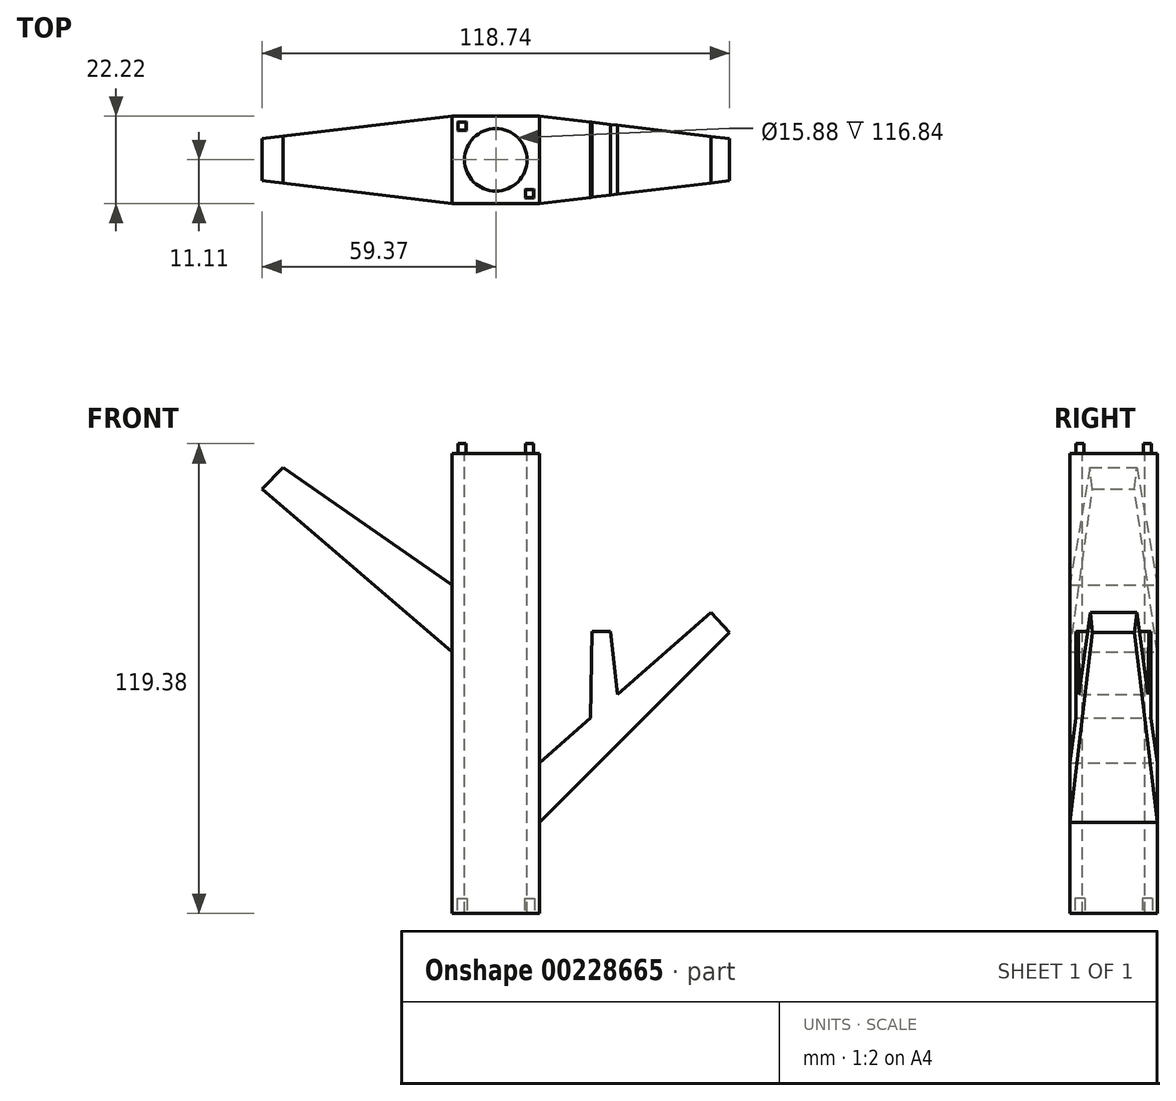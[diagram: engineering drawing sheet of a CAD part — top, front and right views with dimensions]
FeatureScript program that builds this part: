
annotation { "Feature Type Name" : "Feature", "Feature Type Description" : "" }
export const myFeature = defineFeature(function(context is Context, id is Id, definition is map)
    precondition{}
    {
        {
            var Q0;
            Q0=qCreatedBy(makeId("Front.planeOp"),FACE);
            var sketch = newSketch(context, id + "F0", { "sketchPlane" : qUnion([Q0])});
            skLineSegment(sketch, "E0.bottom", {"start": v(11.11, -58.42) * mm, "end": v(-11.11, -58.42) * mm});
            skLineSegment(sketch, "E0.top", {"start": v(11.11, 58.42) * mm, "end": v(-11.11, 58.42) * mm});
            skLineSegment(sketch, "E0.left", {"start": v(11.11, -58.42) * mm, "end": v(11.11, 58.42) * mm});
            skLineSegment(sketch, "E0.right", {"start": v(-11.11, -58.42) * mm, "end": v(-11.11, 58.42) * mm});
            skPoint(sketch, "E0.middle", {"position": v(0, 8.9) * mm});
            skLineSegment(sketch, "E1", {"start": v(0, 17.33) * mm, "end": v(-54.08, 54.94) * mm});
            skLineSegment(sketch, "E2", {"start": v(-54.08, 54.94) * mm, "end": v(-59.37, 49.45) * mm});
            skLineSegment(sketch, "E3", {"start": v(-59.37, 49.45) * mm, "end": v(0, -1.57) * mm});
            skLineSegment(sketch, "E4", {"start": v(0, -1.57) * mm, "end": v(0, 17.33) * mm});
            skLineSegment(sketch, "E5", {"start": v(0, -46.43) * mm, "end": v(59.37, 12.94) * mm});
            skLineSegment(sketch, "E6", {"start": v(59.37, 12.94) * mm, "end": v(54.7, 18.05) * mm});
            skLineSegment(sketch, "E7", {"start": v(54.7, 18.05) * mm, "end": v(0, -29.87) * mm});
            skLineSegment(sketch, "E8", {"start": v(0, -29.87) * mm, "end": v(0, -46.43) * mm});
            skLineSegment(sketch, "E9", {"start": v(24.1, -8.76) * mm, "end": v(24.4, 13.23) * mm});
            skPoint(sketch, "E9.endSnap0", {"position": v(27.35, -5.9) * mm});
            skLineSegment(sketch, "E10", {"start": v(24.4, 13.23) * mm, "end": v(29.13, 13.23) * mm});
            skLineSegment(sketch, "E11", {"start": v(29.13, 13.23) * mm, "end": v(30.88, -2.82) * mm});
            skSolve(sketch);
        }
        {
            var Q0;
            Q0 = qSketchRegion(id + "F0", true);
            extrude(context, id + "F1", {"entities" : qUnion([Q0]), "endBound" : BoundingType.SYMMETRIC, "depth" : 22.22 * mm});
        }
        {
            var Q0;
            Q0=makeQuery(id+"F1.opExtrude","SWEPT_FACE",FACE,{"disambiguationData":[OSD([sQuery(id+"F0.wireOp",EDGE,"E0.top")])]});
            var sketch = newSketch(context, id + "F2", { "sketchPlane" : qUnion([Q0])});
            skCircle(sketch, "E12", {"center": v(0, 0) * mm, "radius": 7.94 * mm});
            skSolve(sketch);
        }
        {
            var Q0;
            Q0 = qSketchRegion(id + "F2", true);
            extrude(context, id + "F3", {"entities" : qUnion([Q0]), "operationType" : NewBodyOperationType.REMOVE, "oppositeDirection" : true, "depth" : 133.1 * mm});
        }
        {
            var Q0;
            Q0=makeQuery(id+"F1.opExtrude","SWEPT_FACE",FACE,{"disambiguationData":[OSD([sQuery(id+"F0.wireOp",EDGE,"E0.top")])]});
            var sketch = newSketch(context, id + "F4", { "sketchPlane" : qUnion([Q0])});
            skLineSegment(sketch, "E13", {"start": v(-11.11, -11.11) * mm, "end": v(-61.55, -5.08) * mm});
            skLineSegment(sketch, "E14", {"start": v(-61.55, -5.08) * mm, "end": v(-61.55, -11.11) * mm});
            skLineSegment(sketch, "E15", {"start": v(-61.55, -11.11) * mm, "end": v(-11.11, -11.11) * mm});
            skLineSegment(sketch, "E16", {"start": v(-11.11, 11.11) * mm, "end": v(-61.55, 5.08) * mm});
            skLineSegment(sketch, "E17", {"start": v(-61.55, 5.08) * mm, "end": v(-61.55, 11.11) * mm});
            skLineSegment(sketch, "E18", {"start": v(-61.55, 11.11) * mm, "end": v(-11.11, 11.11) * mm});
            skLineSegment(sketch, "E19", {"start": v(11.11, -11.11) * mm, "end": v(61.55, -5.08) * mm});
            skLineSegment(sketch, "E20", {"start": v(61.55, -5.08) * mm, "end": v(61.55, -11.11) * mm});
            skLineSegment(sketch, "E21", {"start": v(61.55, -11.11) * mm, "end": v(11.11, -11.11) * mm});
            skLineSegment(sketch, "E22", {"start": v(11.11, 11.11) * mm, "end": v(61.55, 5.08) * mm});
            skLineSegment(sketch, "E23", {"start": v(61.55, 5.08) * mm, "end": v(61.55, 11.11) * mm});
            skLineSegment(sketch, "E24", {"start": v(61.55, 11.11) * mm, "end": v(11.11, 11.11) * mm});
            skSolve(sketch);
        }
        {
            var Q0;
            Q0 = qSketchRegion(id + "F4", true);
            extrude(context, id + "F5", {"entities" : qUnion([Q0]), "operationType" : NewBodyOperationType.REMOVE, "oppositeDirection" : true, "depth" : 135.64 * mm});
        }
        {
            var Q0;
            Q0=makeQuery(id+"F1.opExtrude","SWEPT_FACE",FACE,{"disambiguationData":[OSD([sQuery(id+"F0.wireOp",EDGE,"E0.bottom")])]});
            var sketch = newSketch(context, id + "F6", { "sketchPlane" : qUnion([Q0])});
            skLineSegment(sketch, "E25.bottom", {"start": v(7.3, 7.3) * mm, "end": v(9.84, 7.3) * mm});
            skLineSegment(sketch, "E25.top", {"start": v(7.3, 9.84) * mm, "end": v(9.84, 9.84) * mm});
            skLineSegment(sketch, "E25.left", {"start": v(7.3, 7.3) * mm, "end": v(7.3, 9.84) * mm});
            skLineSegment(sketch, "E25.right", {"start": v(9.84, 7.3) * mm, "end": v(9.84, 9.84) * mm});
            skPoint(sketch, "E25.middle", {"position": v(8.57, 8.57) * mm});
            skLineSegment(sketch, "E26.bottom", {"start": v(-9.84, -9.84) * mm, "end": v(-7.3, -9.84) * mm});
            skLineSegment(sketch, "E26.top", {"start": v(-9.84, -7.3) * mm, "end": v(-7.3, -7.3) * mm});
            skLineSegment(sketch, "E26.left", {"start": v(-9.84, -9.84) * mm, "end": v(-9.84, -7.3) * mm});
            skLineSegment(sketch, "E26.right", {"start": v(-7.3, -9.84) * mm, "end": v(-7.3, -7.3) * mm});
            skPoint(sketch, "E26.middle", {"position": v(-8.57, -8.57) * mm});
            skSolve(sketch);
        }
        {
            var Q0;
            Q0 = qSketchRegion(id + "F6", true);
            extrude(context, id + "F7", {"entities" : qUnion([Q0]), "operationType" : NewBodyOperationType.REMOVE, "oppositeDirection" : true, "depth" : 3.8 * mm});
        }
        {
            var Q0;
            Q0=makeQuery(id+"F1.opExtrude","SWEPT_FACE",FACE,{"disambiguationData":[OSD([sQuery(id+"F0.wireOp",EDGE,"E0.top")])]});
            var sketch = newSketch(context, id + "F8", { "sketchPlane" : qUnion([Q0])});
            skLineSegment(sketch, "E27.bottom", {"start": v(7.56, -9.59) * mm, "end": v(9.59, -9.59) * mm});
            skLineSegment(sketch, "E27.top", {"start": v(7.56, -7.56) * mm, "end": v(9.59, -7.56) * mm});
            skLineSegment(sketch, "E27.left", {"start": v(7.56, -9.59) * mm, "end": v(7.56, -7.56) * mm});
            skLineSegment(sketch, "E27.right", {"start": v(9.59, -9.59) * mm, "end": v(9.59, -7.56) * mm});
            skPoint(sketch, "E27.middle", {"position": v(8.57, -8.57) * mm});
            skLineSegment(sketch, "E28.bottom", {"start": v(-9.59, 7.56) * mm, "end": v(-7.56, 7.56) * mm});
            skLineSegment(sketch, "E28.top", {"start": v(-9.59, 9.59) * mm, "end": v(-7.56, 9.59) * mm});
            skLineSegment(sketch, "E28.left", {"start": v(-9.59, 7.56) * mm, "end": v(-9.59, 9.59) * mm});
            skLineSegment(sketch, "E28.right", {"start": v(-7.56, 7.56) * mm, "end": v(-7.56, 9.59) * mm});
            skPoint(sketch, "E28.middle", {"position": v(-8.57, 8.57) * mm});
            skSolve(sketch);
        }
        {
            var Q0;
            Q0 = qSketchRegion(id + "F8", true);
            extrude(context, id + "F9", {"entities" : qUnion([Q0]), "operationType" : NewBodyOperationType.ADD, "depth" : 2.54 * mm});
        }
    });
